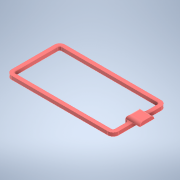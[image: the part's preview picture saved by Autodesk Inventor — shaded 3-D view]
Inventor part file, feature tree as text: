
AUTODESK INVENTOR PART (.ipt)
format: ipt  version: 2022 (Build 260153000, 153)  size: 151,552 bytes
history: native  units: mm
features: extrude x2, fillet x2, sketch x2
ambient origin geometry x8: Origin, YZ Plane, XZ Plane, XY Plane, X Axis, Y Axis, Z Axis, Center Point
bodies: Solid1 (feature_tree)
feature tree (6):
  extrude  "Extrusion1"  Depth=60.0mm
  extrude  "Extrusion2"  Depth=3.0mm
  fillet  "Fillet1"  Radius=2.0mm
  fillet  "Fillet2"  Radius=2.0mm
  sketch  "Sketch1"  dims[d0=30.0mm d1=60.0mm]
  sketch  "Sketch2"  dims[d2=3.0mm d3=3.0mm d4=2.0mm d5=2.0mm d6=0.0mm d7=8.0mm d8=2.0mm d9=0.0mm d10=2.0mm d11=2.0mm]
